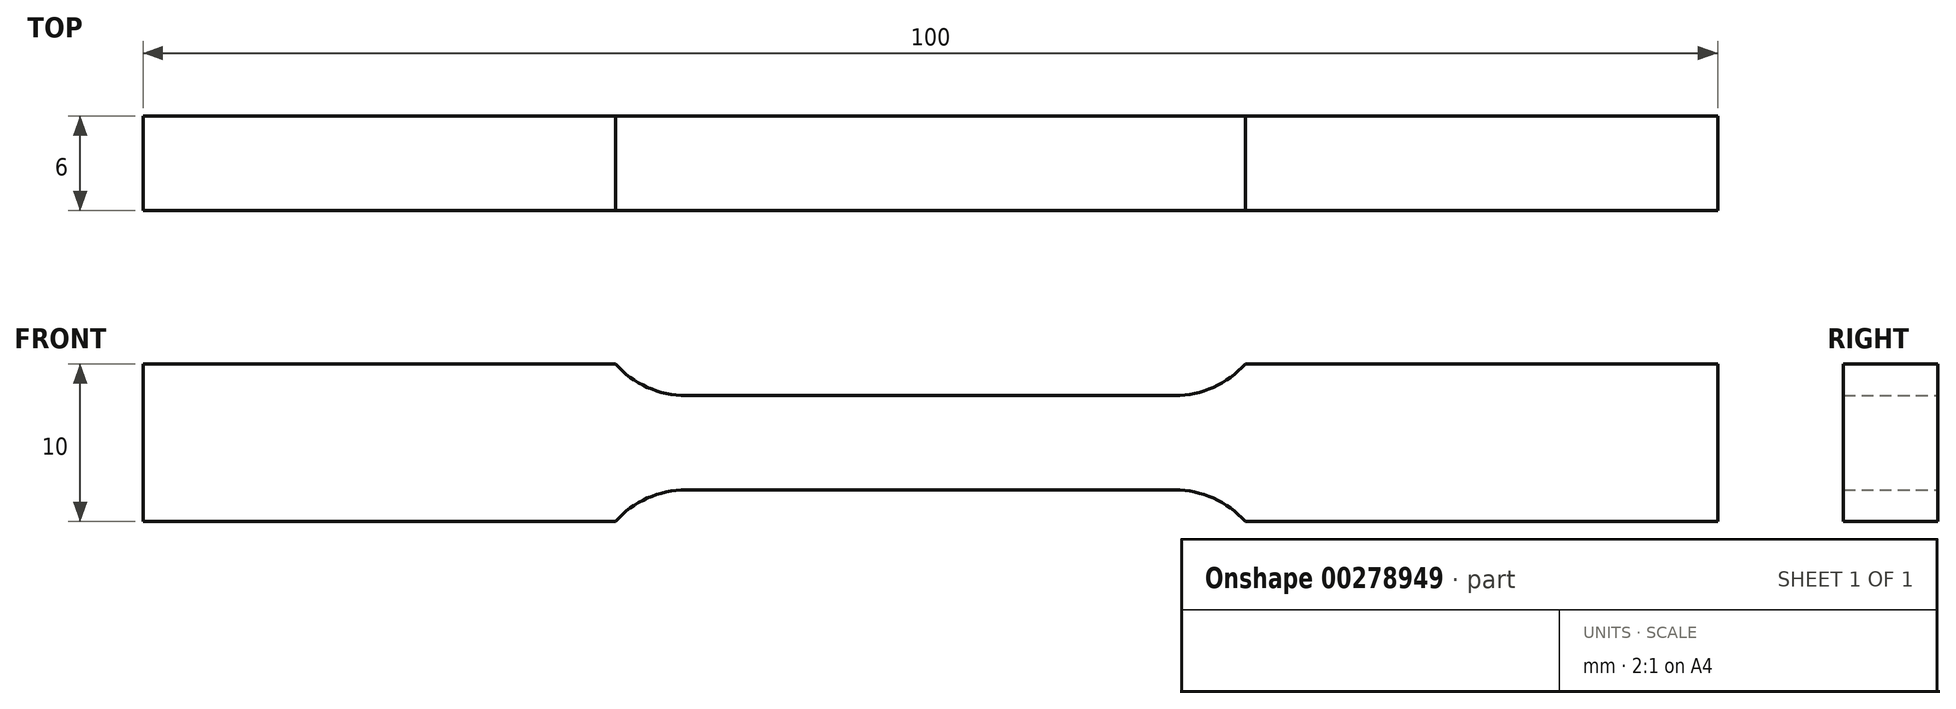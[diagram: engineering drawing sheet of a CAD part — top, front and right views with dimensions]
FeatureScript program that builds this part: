
annotation { "Feature Type Name" : "Feature", "Feature Type Description" : "" }
export const myFeature = defineFeature(function(context is Context, id is Id, definition is map)
    precondition{}
    {
        {
            var Q0;
            Q0=qCreatedBy(makeId("Front.planeOp"),FACE);
            var sketch = newSketch(context, id + "F0", { "sketchPlane" : qUnion([Q0])});
            skLineSegment(sketch, "E0", {"start": v(0, 3) * mm, "end": v(15.53, 3) * mm});
            skArc(sketch, "E1", {"start": v(15.53, 3) * mm, "mid": v(17.98, 3.52) * mm, "end": v(20, 5) * mm});
            skLineSegment(sketch, "E2", {"start": v(20, 5) * mm, "end": v(50, 5) * mm});
            skLineSegment(sketch, "E3", {"start": v(50, 5) * mm, "end": v(50, 0) * mm});
            skLineSegment(sketch, "E4.MirrorCS", {"start": v(0, -3) * mm, "end": v(15.53, -3) * mm});
            skArc(sketch, "E5.MirrorCS", {"start": v(15.53, -3) * mm, "mid": v(17.98, -3.52) * mm, "end": v(20, -5) * mm});
            skLineSegment(sketch, "E6.MirrorCS", {"start": v(50, -5) * mm, "end": v(50, 0) * mm});
            skLineSegment(sketch, "E7.MirrorCS", {"start": v(20, -5) * mm, "end": v(50, -5) * mm});
            skArc(sketch, "E8.MirrorCS", {"start": v(-15.53, -3) * mm, "mid": v(-17.98, -3.52) * mm, "end": v(-20, -5) * mm});
            skArc(sketch, "E9.MirrorCS", {"start": v(-15.53, 3) * mm, "mid": v(-17.98, 3.52) * mm, "end": v(-20, 5) * mm});
            skLineSegment(sketch, "E10.MirrorCS", {"start": v(0, 3) * mm, "end": v(-15.53, 3) * mm});
            skLineSegment(sketch, "E11.MirrorCS", {"start": v(-50, -5) * mm, "end": v(-50, 0) * mm});
            skLineSegment(sketch, "E12.MirrorCS", {"start": v(-20, -5) * mm, "end": v(-50, -5) * mm});
            skLineSegment(sketch, "E13.MirrorCS", {"start": v(-20, 5) * mm, "end": v(-50, 5) * mm});
            skLineSegment(sketch, "E14.MirrorCS", {"start": v(0, -3) * mm, "end": v(-15.53, -3) * mm});
            skLineSegment(sketch, "E15.MirrorCS", {"start": v(-50, 5) * mm, "end": v(-50, 0) * mm});
            skSolve(sketch);
        }
        {
            var Q0;
            Q0=makeQuery(id+"F0.imprint","IMPRINT",FACE,{"disambiguationData":[TD([[makeQuery(id+"F0.imprint","IMPRINT",EDGE,{"derivedFrom":sQuery(id+"F0.wireOp",EDGE,"E6.MirrorCS")}),1.0]])]});
            extrude(context, id + "F1", {"entities" : qUnion([Q0]), "endBound" : BoundingType.SYMMETRIC, "depth" : 6 * mm});
        }
    });
